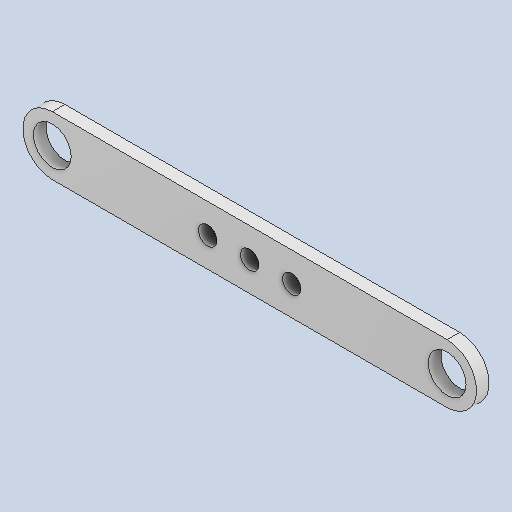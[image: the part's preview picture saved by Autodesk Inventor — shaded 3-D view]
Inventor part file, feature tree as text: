
AUTODESK INVENTOR PART (.ipt)
format: ipt  version: 2025.1 (Build 291241000, 241)  size: 175,104 bytes
history: native  units: mm
features: other x2, extrude x2, sketch x2
ambient origin geometry x8: Origin, YZ Plane, XZ Plane, XY Plane, X Axis, Y Axis, Z Axis, Center Point
bodies: Body1 (feature_tree)
feature tree (6):
  other  "ソリッド1"
  extrude  "押し出し1"  Depth=7.0mm
  extrude  "押し出し2"  Depth=47.0mm
  sketch  "スケッチ1"
  sketch  "スケッチ2"
  other  "スケッチ矩形状パターン1"
